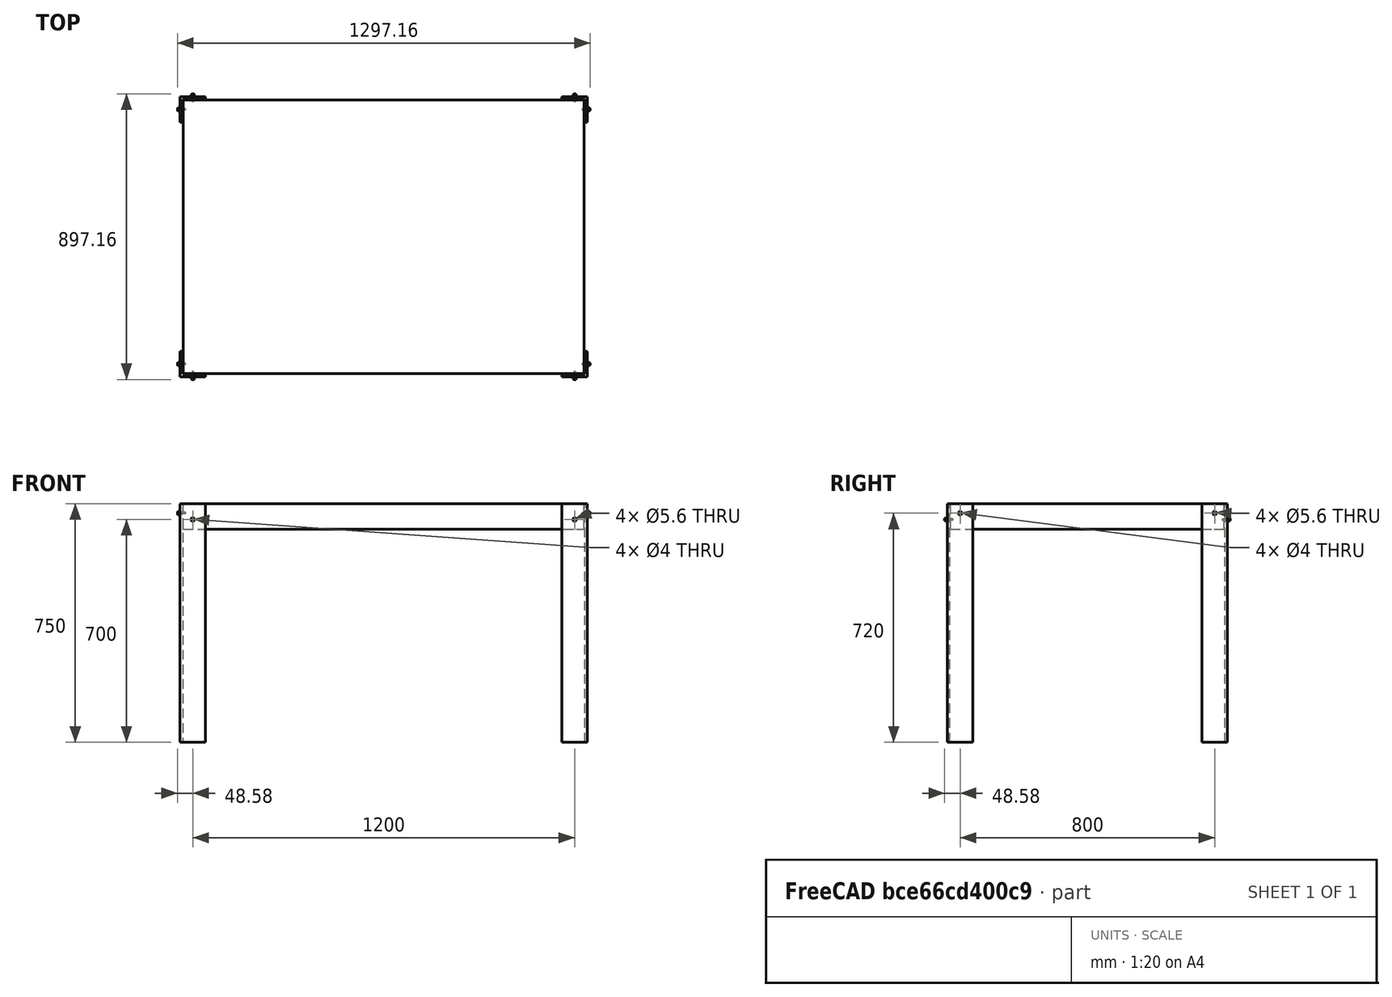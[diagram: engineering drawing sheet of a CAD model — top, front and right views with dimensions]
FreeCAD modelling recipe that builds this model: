
FCSTD DOCUMENT  (FreeCAD 0.21R33771 (Git))
Label: table
License: All rights reserved
LicenseURL: https://en.wikipedia.org/wiki/All_rights_reserved
objects: Part::Cut×12, Part::Box×9, Part::FeaturePython×8, Part::Cylinder×4
note: 33 computed .brp shape members not serialized (recipe doc carries the construction recipe); baked Part::Feature solids carry a one-line shape summary decoded from their .brp

FEATURE [Part::Box] Box  label="Cube"
  AttacherType = Attacher::AttachEngine3D
  Height = 750
  Length = 80
  Width = 80
FEATURE [Part::Box] Box001  label="Cube001"
  AttacherType = Attacher::AttachEngine3D
  Height = 750
  Length = 80
  Placement = pos=(8,8,0) rot=(0,0,1;0rad)
  Width = 80
FEATURE [Part::Cut] Cut
  Base = -> Box
  Tool = -> Box001
FEATURE [Part::Box] Box002  label="Cube002"
  AttacherType = Attacher::AttachEngine3D
  Height = 750
  Length = 80
  Placement = pos=(0,800,0) rot=(0,0,1;0rad)
  Width = 80
FEATURE [Part::Box] Box003  label="Cube003"
  AttacherType = Attacher::AttachEngine3D
  Height = 750
  Length = 80
  Placement = pos=(8,792,0) rot=(0,0,1;0rad)
  Width = 80
FEATURE [Part::Box] Box004  label="Cube004"
  AttacherType = Attacher::AttachEngine3D
  Height = 750
  Length = 80
  Placement = pos=(1200,0,0) rot=(0,0,1;0rad)
  Width = 80
FEATURE [Part::Box] Box005  label="Cube005"
  AttacherType = Attacher::AttachEngine3D
  Height = 750
  Length = 80
  Placement = pos=(1192,8,0) rot=(0,0,1;0rad)
  Width = 80
FEATURE [Part::Box] Box006  label="Cube006"
  AttacherType = Attacher::AttachEngine3D
  Height = 750
  Length = 80
  Placement = pos=(1200,800,0) rot=(0,0,1;0rad)
  Width = 80
FEATURE [Part::Box] Box007  label="Cube007"
  AttacherType = Attacher::AttachEngine3D
  Height = 750
  Length = 80
  Placement = pos=(1192,792,0) rot=(0,0,1;0rad)
  Width = 80
FEATURE [Part::Cut] Cut001
  Base = -> Box002
  Tool = -> Box003
FEATURE [Part::Cut] Cut002
  Base = -> Box006
  Tool = -> Box007
FEATURE [Part::Cut] Cut003
  Base = -> Box004
  Tool = -> Box005
FEATURE [Part::Cylinder] Cylinder
  Angle = 360
  AttacherType = Attacher::AttachEngine3D
  FirstAngle = 0
  Height = 1300
  Placement = pos=(-10,40,720) rot=(0,1,0;1.5708rad)
  Radius = 2
  SecondAngle = 0
FEATURE [Part::Cylinder] Cylinder001
  Angle = 360
  AttacherType = Attacher::AttachEngine3D
  FirstAngle = 0
  Height = 1300
  Placement = pos=(-10,840,720) rot=(0,1,0;1.5708rad)
  Radius = 2
  SecondAngle = 0
FEATURE [Part::Cylinder] Cylinder002
  Angle = 360
  AttacherType = Attacher::AttachEngine3D
  FirstAngle = 0
  Height = 900
  Placement = pos=(40,-10,700) rot=(-1,0,0;1.5708rad)
  Radius = 2
  SecondAngle = 0
FEATURE [Part::Cylinder] Cylinder003
  Angle = 360
  AttacherType = Attacher::AttachEngine3D
  FirstAngle = 0
  Height = 900
  Placement = pos=(1240,-10,700) rot=(-1,0,0;1.5708rad)
  Radius = 2
  SecondAngle = 0
FEATURE [Part::Cut] Cut004
  Base = -> Cut003
  Tool = -> Cylinder003
FEATURE [Part::Cut] Cut005
  Base = -> Cut002
  Tool = -> Cylinder003
FEATURE [Part::Cut] Cut006  label="leg_rear_right"
  Base = -> Cut005
  Tool = -> Cylinder001
FEATURE [Part::Cut] Cut007
  Base = -> Cut001
  Tool = -> Cylinder001
FEATURE [Part::Cut] Cut008  label="leg_rear_left"
  Base = -> Cut007
  Tool = -> Cylinder002
FEATURE [Part::Cut] Cut009
  Base = -> Cut
  Tool = -> Cylinder002
FEATURE [Part::Cut] Cut010  label="leg_front_left"
  Base = -> Cut009
  Tool = -> Cylinder
FEATURE [Part::Cut] Cut011  label="leg_front_right"
  Base = -> Cut004
  Tool = -> Cylinder
FEATURE [Part::Box] Box008  label="table_top"
  AttacherType = Attacher::AttachEngine3D
  Height = 80
  Length = 1260
  Placement = pos=(10,10,670) rot=(0,0,1;0rad)
  Width = 860
FEATURE [Part::FeaturePython] Screw  label="M5x20-Screw"  # WARN: FeaturePython — macro-defined, semantics opaque (R4)
  BaseObject = -> Cut010 [Edge5]
  Diameter = 1
  Invert = false
  LeftHanded = false
  Length = 3
  LengthCustom = 20
  MatchOuter = false
  Offset = 4
  OffsetAngle = 0
  Placement = pos=(-4,40,720) rot=(0,-1,0;1.5708rad)
  Thread = false
  Type = 44
FEATURE [Part::FeaturePython] Screw001  label="M5x20-Screw011"  # WARN: FeaturePython — macro-defined, semantics opaque (R4)
  BaseObject = -> Cut010 [Edge9]
  Diameter = 1
  Invert = false
  LeftHanded = false
  Length = 3
  LengthCustom = 20
  MatchOuter = false
  Offset = 4
  OffsetAngle = 0
  Placement = pos=(40,-4,700) rot=(1,0,0;1.5708rad)
  Thread = false
  Type = 44
FEATURE [Part::FeaturePython] Screw002  label="M5x20-Screw012"  # WARN: FeaturePython — macro-defined, semantics opaque (R4)
  BaseObject = -> Cut011 [Edge18]
  Diameter = 1
  Invert = false
  LeftHanded = false
  Length = 3
  LengthCustom = 20
  MatchOuter = false
  Offset = 4
  OffsetAngle = 0
  Placement = pos=(1240,-4,700) rot=(1,0,0;1.5708rad)
  Thread = false
  Type = 44
FEATURE [Part::FeaturePython] Screw003  label="M5x20-Screw013"  # WARN: FeaturePython — macro-defined, semantics opaque (R4)
  BaseObject = -> Cut011 [Edge22]
  Diameter = 1
  Invert = true
  LeftHanded = false
  Length = 3
  LengthCustom = 20
  MatchOuter = false
  Offset = 4
  OffsetAngle = 0
  Placement = pos=(1284,40,720) rot=(0,1,0;1.5708rad)
  Thread = false
  Type = 44
FEATURE [Part::FeaturePython] Screw004  label="M5x20-Screw014"  # WARN: FeaturePython — macro-defined, semantics opaque (R4)
  BaseObject = -> Cut006 [Edge20]
  Diameter = 1
  Invert = true
  LeftHanded = false
  Length = 3
  LengthCustom = 20
  MatchOuter = false
  Offset = 4
  OffsetAngle = 0
  Placement = pos=(1284,840,720) rot=(0,1,0;1.5708rad)
  Thread = false
  Type = 44
FEATURE [Part::FeaturePython] Screw005  label="M5x20-Screw015"  # WARN: FeaturePython — macro-defined, semantics opaque (R4)
  BaseObject = -> Cut006 [Edge12]
  Diameter = 1
  Invert = true
  LeftHanded = false
  Length = 3
  LengthCustom = 20
  MatchOuter = false
  Offset = 4
  OffsetAngle = 0
  Placement = pos=(1240,884,700) rot=(-1,0,0;1.5708rad)
  Thread = false
  Type = 44
FEATURE [Part::FeaturePython] Screw006  label="M5x20-Screw016"  # WARN: FeaturePython — macro-defined, semantics opaque (R4)
  BaseObject = -> Cut008 [Edge18]
  Diameter = 1
  Invert = true
  LeftHanded = false
  Length = 3
  LengthCustom = 20
  MatchOuter = false
  Offset = 4
  OffsetAngle = 0
  Placement = pos=(40,884,700) rot=(-1,0,0;1.5708rad)
  Thread = false
  Type = 44
FEATURE [Part::FeaturePython] Screw007  label="M5x20-Screw017"  # WARN: FeaturePython — macro-defined, semantics opaque (R4)
  BaseObject = -> Cut008 [Edge5]
  Diameter = 1
  Invert = false
  LeftHanded = false
  Length = 3
  LengthCustom = 20
  MatchOuter = false
  Offset = 4
  OffsetAngle = 0
  Placement = pos=(-4,840,720) rot=(0,-1,0;1.5708rad)
  Thread = false
  Type = 44
